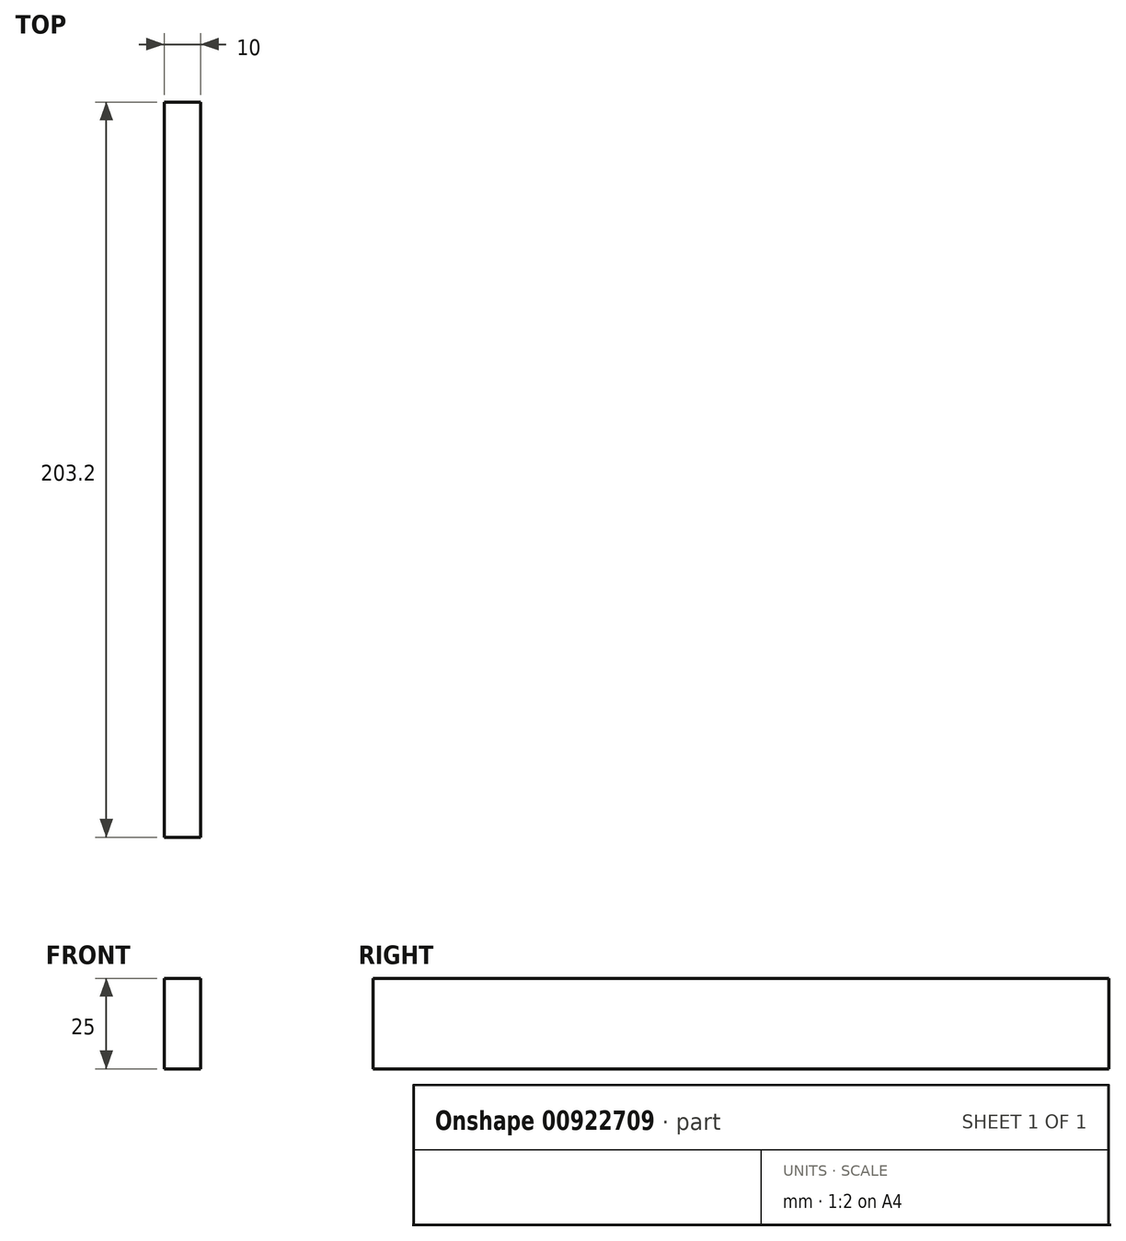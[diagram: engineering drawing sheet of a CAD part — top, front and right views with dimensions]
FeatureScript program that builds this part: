
annotation { "Feature Type Name" : "Feature", "Feature Type Description" : "" }
export const myFeature = defineFeature(function(context is Context, id is Id, definition is map)
    precondition{}
    {
        {
            var Q0;
            Q0=qCreatedBy(makeId("Front.planeOp"),FACE);
            var sketch = newSketch(context, id + "F0", { "sketchPlane" : qUnion([Q0])});
            skLineSegment(sketch, "E0.bottom", {"start": v(0, 0) * mm, "end": v(10, 0) * mm});
            skLineSegment(sketch, "E0.top", {"start": v(0, 25) * mm, "end": v(10, 25) * mm});
            skLineSegment(sketch, "E0.left", {"start": v(0, 0) * mm, "end": v(0, 25) * mm});
            skLineSegment(sketch, "E0.right", {"start": v(10, 0) * mm, "end": v(10, 25) * mm});
            skSolve(sketch);
        }
        {
            var Q0;
            Q0=makeQuery(id+"F0.imprint","IMPRINT",FACE,{"disambiguationData":[TD([[makeQuery(id+"F0.imprint","IMPRINT",EDGE,{"derivedFrom":sQuery(id+"F0.wireOp",EDGE,"E0.bottom")}),1.0]])]});
            extrude(context, id + "F1", {"entities" : qUnion([Q0]), "depth" : 203.2 * mm, "offsetDistance" : 25.4 * mm});
        }
    });
